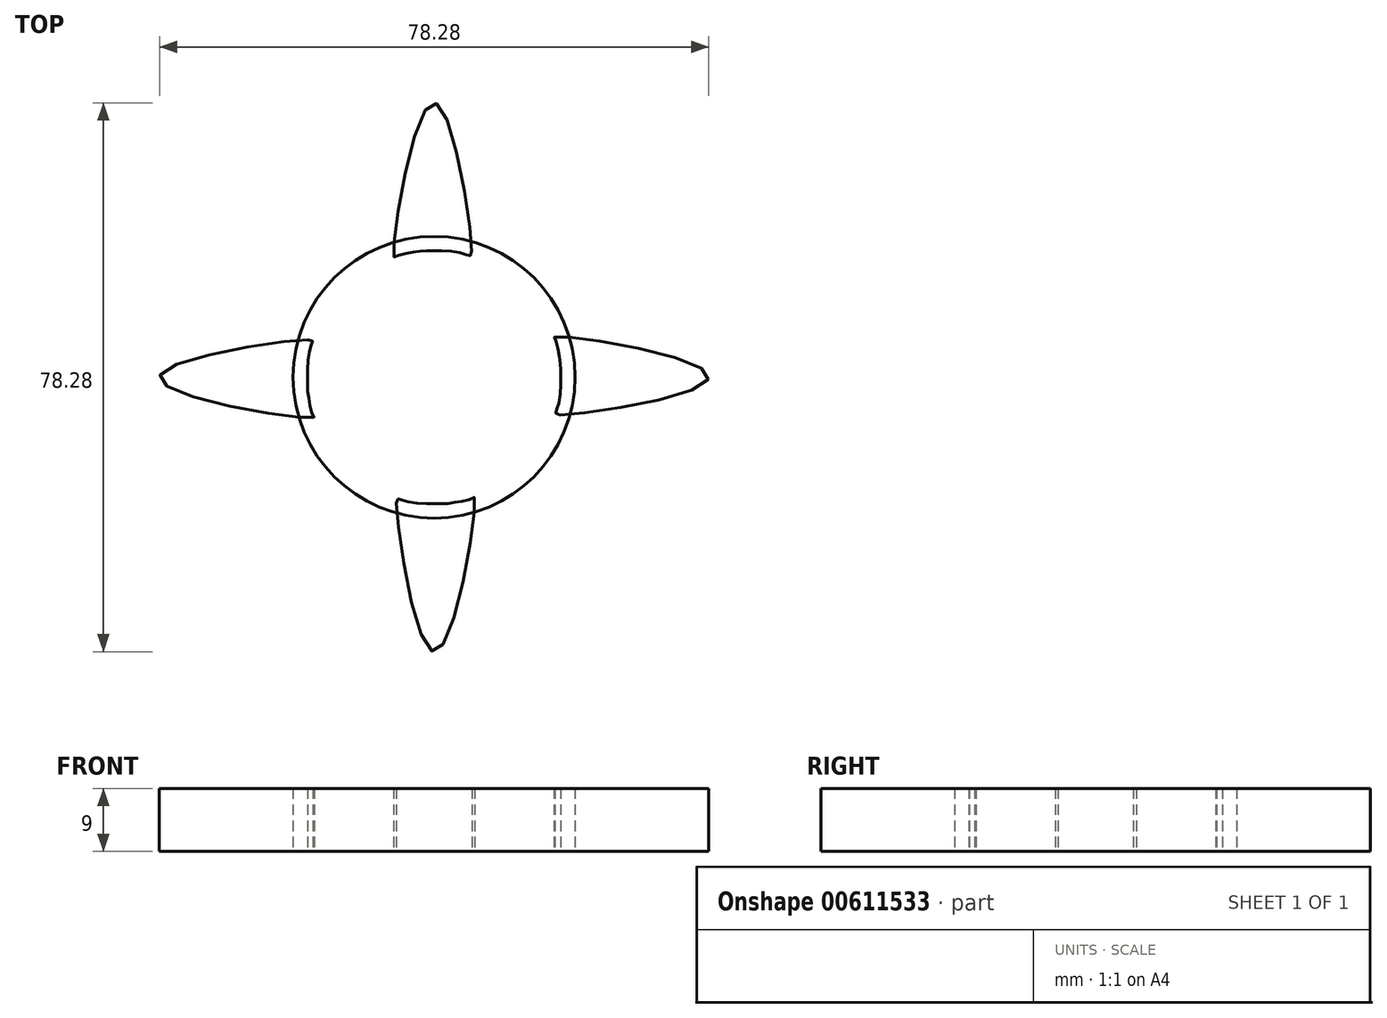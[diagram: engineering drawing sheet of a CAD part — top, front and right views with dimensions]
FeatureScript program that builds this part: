
annotation { "Feature Type Name" : "Feature", "Feature Type Description" : "" }
export const myFeature = defineFeature(function(context is Context, id is Id, definition is map)
    precondition{}
    {
        {
            var Q0;
            Q0=qCreatedBy(makeId("Top.planeOp"),FACE);
            var sketch = newSketch(context, id + "F0", { "sketchPlane" : qUnion([Q0])});
            skCircle(sketch, "E0", {"center": v(0, 0) * mm, "radius": 20.1 * mm});
            skSolve(sketch);
        }
        {
            var Q0;
            Q0=qCreatedBy(makeId("Top.planeOp"),FACE);
            var sketch = newSketch(context, id + "F1", { "sketchPlane" : qUnion([Q0])});
            skFitSpline(sketch, "E1", {"points": [v(-19.5, 4.56) * mm, v(-19.9, 3.1) * mm, v(-20.03, 0.6) * mm, v(-20.05, -0.91) * mm, v(-19.97, -2.23) * mm, v(-19.74, -3.6) * mm, v(-19.32, -5.23) * mm, v(-19.18, -5.72) * mm, v(-41.14, 0) * mm, v(-19.27, 5.32) * mm, v(-19.38, 5.08) * mm, v(-19.5, 4.56) * mm]});
            skSolve(sketch);
        }
        {
            var Q0;
            Q0=makeQuery(id+"F0.imprint","IMPRINT",FACE,{"disambiguationData":[TD([[makeQuery(id+"F0.imprint","IMPRINT",EDGE,{"derivedFrom":sQuery(id+"F0.wireOp",EDGE,"E0")}),1.0]])]});
            extrude(context, id + "F2", {"entities" : qUnion([Q0]), "endBound" : BoundingType.SYMMETRIC, "depth" : 9 * mm, "offsetDistance" : 25 * mm});
        }
        {
            var Q0;
            Q0=makeQuery(id+"F1.imprint","IMPRINT",FACE,{"disambiguationData":[TD([[makeQuery(id+"F1.imprint","IMPRINT",EDGE,{"derivedFrom":sQuery(id+"F1.wireOp",EDGE,"E1")}),-1.0]])]});
            extrude(context, id + "F3", {"entities" : qUnion([Q0]), "endBound" : BoundingType.SYMMETRIC, "depth" : 9 * mm, "offsetDistance" : 25 * mm});
        }
        {
            var Q0;
            Q0=makeQuery(id+"F3.opExtrude","SWEPT_BODY",BODY,{"disambiguationData":[OSD([sQuery(id+"F1.wireOp",EDGE,"E1")])]});
            var Q1;
            Q1=makeQuery(id+"F2.opExtrude","CAP_EDGE",EDGE,{"disambiguationData":[OSD([sQuery(id+"F0.wireOp",EDGE,"E0")])],"isStart":false});
            circularPattern(context, id + "F4", {"entities" : qUnion([Q0]), "axis" : qUnion([Q1]), "angle" : 360 * degree, "instanceCount" : 4, "equalSpace" : true});
        }
        {
            var Q0;
            Q0=makeQuery(id+"F2.opExtrude","SWEPT_BODY",BODY,{"disambiguationData":[OSD([sQuery(id+"F0.wireOp",EDGE,"E0")])]});
            var Q1;
            Q1=makeQuery(id+"F4.opPattern","COPY",BODY,{"derivedFrom":makeQuery(id+"F3.opExtrude","SWEPT_BODY",BODY,{"disambiguationData":[OSD([sQuery(id+"F1.wireOp",EDGE,"E1")])]}),"instanceName":"1"});
            var Q2;
            Q2=makeQuery(id+"F4.opPattern","COPY",BODY,{"derivedFrom":makeQuery(id+"F3.opExtrude","SWEPT_BODY",BODY,{"disambiguationData":[OSD([sQuery(id+"F1.wireOp",EDGE,"E1")])]}),"instanceName":"2"});
            var Q3;
            Q3=makeQuery(id+"F3.opExtrude","SWEPT_BODY",BODY,{"disambiguationData":[OSD([sQuery(id+"F1.wireOp",EDGE,"E1")])]});
            var Q4;
            Q4=makeQuery(id+"F4.opPattern","COPY",BODY,{"derivedFrom":makeQuery(id+"F3.opExtrude","SWEPT_BODY",BODY,{"disambiguationData":[OSD([sQuery(id+"F1.wireOp",EDGE,"E1")])]}),"instanceName":"3"});
            transform(context, id + "F5", {"entities" : qUnion([Q0, Q1, Q2, Q3, Q4]), "transformType" : TransformType.TRANSLATION_3D, "dx" : 0 * mm, "dy" : 0 * mm, "dz" : 3.5 * mm, "makeCopy" : false});
        }
        {
            var Q0;
            Q0=makeQuery(id+"F4.opPattern","COPY",BODY,{"derivedFrom":makeQuery(id+"F3.opExtrude","SWEPT_BODY",BODY,{"disambiguationData":[OSD([sQuery(id+"F1.wireOp",EDGE,"E1")])]}),"instanceName":"1"});
            transform(context, id + "F6", {"entities" : qUnion([Q0]), "transformType" : TransformType.TRANSLATION_3D, "dx" : 0 * mm, "dy" : 2 * mm, "dz" : 0 * mm, "makeCopy" : false});
        }
        {
            var Q0;
            Q0=makeQuery(id+"F3.opExtrude","SWEPT_BODY",BODY,{"disambiguationData":[OSD([sQuery(id+"F1.wireOp",EDGE,"E1")])]});
            transform(context, id + "F7", {"entities" : qUnion([Q0]), "transformType" : TransformType.TRANSLATION_3D, "dx" : 2 * mm, "dy" : 0 * mm, "dz" : 0 * mm, "makeCopy" : false});
        }
        {
            var Q0;
            Q0=makeQuery(id+"F4.opPattern","COPY",BODY,{"derivedFrom":makeQuery(id+"F3.opExtrude","SWEPT_BODY",BODY,{"disambiguationData":[OSD([sQuery(id+"F1.wireOp",EDGE,"E1")])]}),"instanceName":"2"});
            transform(context, id + "F8", {"entities" : qUnion([Q0]), "transformType" : TransformType.TRANSLATION_3D, "dx" : -2 * mm, "dy" : 0 * mm, "dz" : 0 * mm, "makeCopy" : false});
        }
        {
            var Q0;
            Q0=makeQuery(id+"F4.opPattern","COPY",BODY,{"derivedFrom":makeQuery(id+"F3.opExtrude","SWEPT_BODY",BODY,{"disambiguationData":[OSD([sQuery(id+"F1.wireOp",EDGE,"E1")])]}),"instanceName":"3"});
            transform(context, id + "F9", {"entities" : qUnion([Q0]), "transformType" : TransformType.TRANSLATION_3D, "dx" : 0 * mm, "dy" : -2 * mm, "dz" : 0 * mm, "makeCopy" : false});
        }
    });
